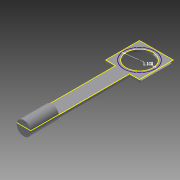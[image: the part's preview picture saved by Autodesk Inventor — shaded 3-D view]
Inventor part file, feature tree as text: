
AUTODESK INVENTOR PART (.ipt)
format: ipt  version: 2014 SP2 (Build 180246200, 246)  size: 131,584 bytes
history: native  units: in
note: dims shown in document units (in); Inventor stores cm internally (conversion verified against a paired STEP export)
features: extrude x5, sketch x5, projected_geometry x1
ambient origin geometry x8: Origin, YZ Plane, XZ Plane, XY Plane, X Axis, Y Axis, Z Axis, Center Point
bodies: Solid1 (feature_tree)
feature tree (11):
  extrude  "Extrusion1"  Depth=0.1in TaperAngle=0.0deg
  extrude  "Extrusion2"  Depth=2.5in TaperAngle=0.0deg
  extrude  "Extrusion5"  Depth=1.0in TaperAngle=0.0deg
  extrude  "Extrusion7"  Depth=0.06in
  extrude  "Extrusion8"  Depth=1.1in
  sketch  "Sketch9"  dims[d37=0.6in d38=0.0in d39=0.95in d40=1.25in d41=0.0in d42=1.1in]
  sketch  "Sketch2"  dims[d0=1.2in d1=0.1in d2=0.0in]
  sketch  "Sketch5"  dims[d3=1.2in d4=2.5in d5=0.0in]
  sketch  "Sketch7"  dims[d14=0.5in d15=1.0in d16=0.0in]
  sketch  "Sketch8"  dims[d35=1.1in d36=0.06in]
  projected_geometry  "Project Cut Edges1"
